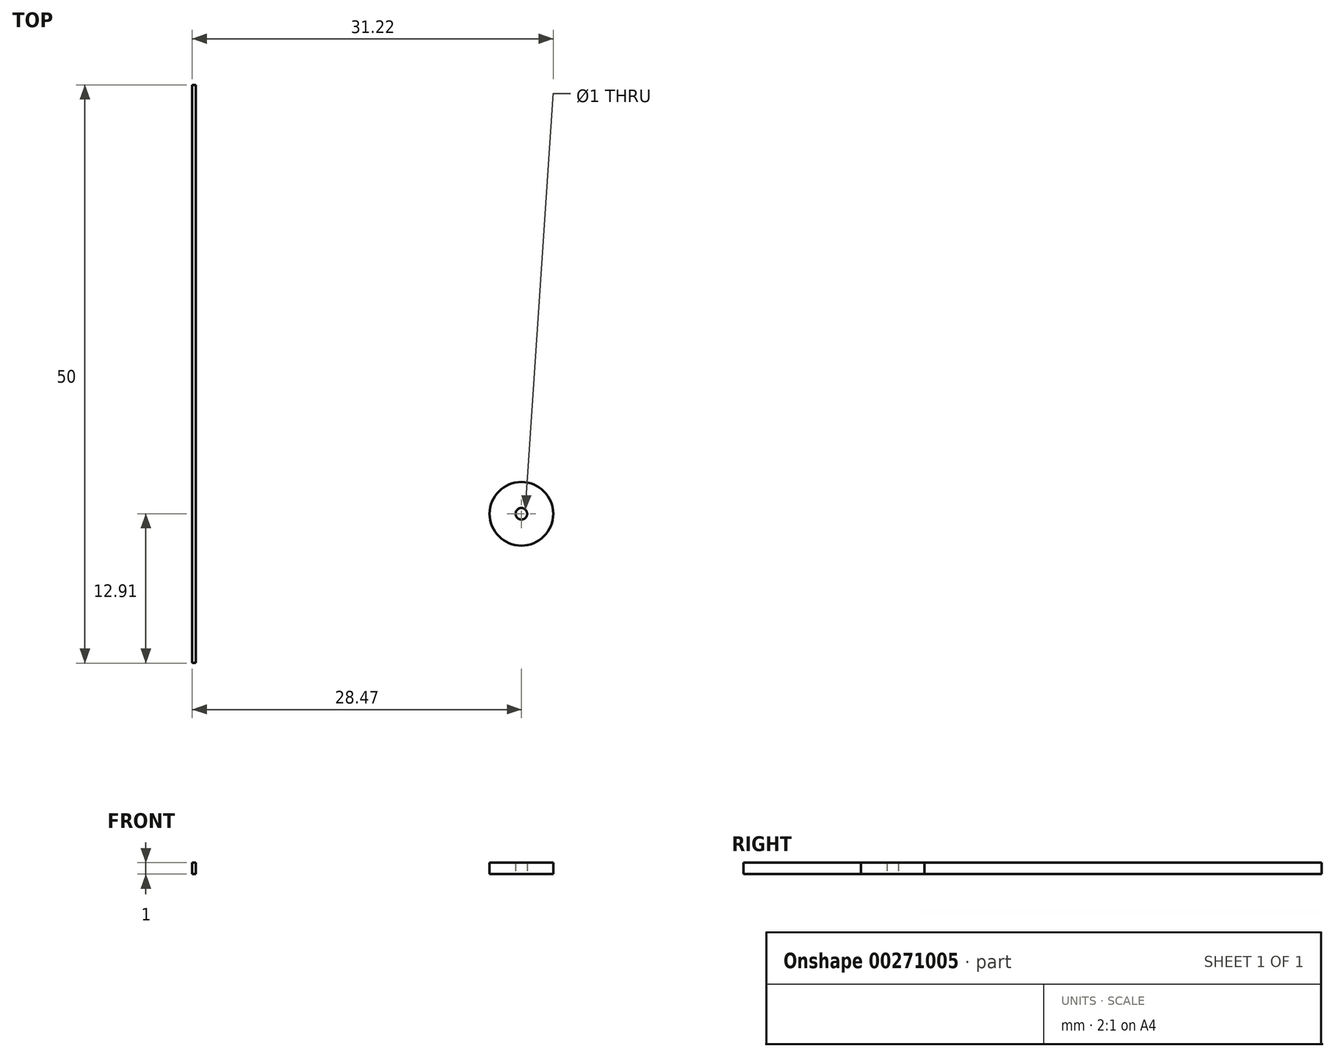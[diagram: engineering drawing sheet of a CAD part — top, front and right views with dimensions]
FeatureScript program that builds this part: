
annotation { "Feature Type Name" : "Feature", "Feature Type Description" : "" }
export const myFeature = defineFeature(function(context is Context, id is Id, definition is map)
    precondition{}
    {
        {
            var Q0;
            Q0=qCreatedBy(makeId("Top.planeOp"),FACE);
            var sketch = newSketch(context, id + "F0", { "sketchPlane" : qUnion([Q0])});
            skCircle(sketch, "E0", {"center": v(0, 0) * mm, "radius": 2.75 * mm});
            skCircle(sketch, "E1", {"center": v(0, 0) * mm, "radius": 0.5 * mm});
            skLineSegment(sketch, "E2.bottom", {"start": v(-28.17, -12.9) * mm, "end": v(-28.47, -12.9) * mm});
            skLineSegment(sketch, "E2.top", {"start": v(-28.17, 37.1) * mm, "end": v(-28.47, 37.1) * mm});
            skLineSegment(sketch, "E2.left", {"start": v(-28.17, -12.9) * mm, "end": v(-28.17, 37.1) * mm});
            skLineSegment(sketch, "E2.right", {"start": v(-28.47, -12.9) * mm, "end": v(-28.47, 37.1) * mm});
            skSolve(sketch);
        }
        {
            var Q0;
            Q0 = qSketchRegion(id + "F0", true);
            extrude(context, id + "F1", {"entities" : qUnion([Q0]), "depth" : 1 * mm, "offsetDistance" : 25 * mm});
        }
    });
